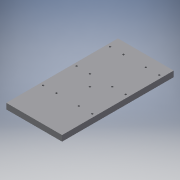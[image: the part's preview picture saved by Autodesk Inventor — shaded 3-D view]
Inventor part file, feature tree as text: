
AUTODESK INVENTOR PART (.ipt)
format: ipt  version: 2018 (Build 220112000, 112)  size: 130,560 bytes
history: native  units: mm
features: sketch x4, hole x2, other x1, extrude x1
ambient origin geometry x8: Origin, YZ Plane, XZ Plane, XY Plane, X Axis, Y Axis, Z Axis, Center Point
bodies: Body1 (feature_tree)
feature tree (8):
  other  "Sólido1"
  extrude  "Extrusão1"  Depth=250.0mm
  sketch  "Esboço3"  dims[d2=12.7mm d3=0.0mm]
  hole  "Furo1"  [1 undecoded]
  hole  "Furo2"  [1 undecoded]
  sketch  "Esboço1"  dims[d0=125.0mm d1=250.0mm]
  sketch  "Esboço4"  dims[d4=4.134mm d5=10.0mm d6=4.0mm d7=2.0mm d8=90.0deg d9=14.2mm d10=20.594885mm d11=4.0mm]
  sketch  "Esboço5"  dims[d12=30.0mm d14=28.0mm d15=30.0mm d17=28.0mm d20=4.134mm d21=10.0mm d22=4.0mm d23=2.0mm d24=90.0deg d25=15.0mm d26=20.594885mm d28=62.5mm]
note: 2 required parameter values undecoded (feature->parameter linkage not recoverable at this tier; creation-order binding heuristic only, values carry confidence <= 0.55)
